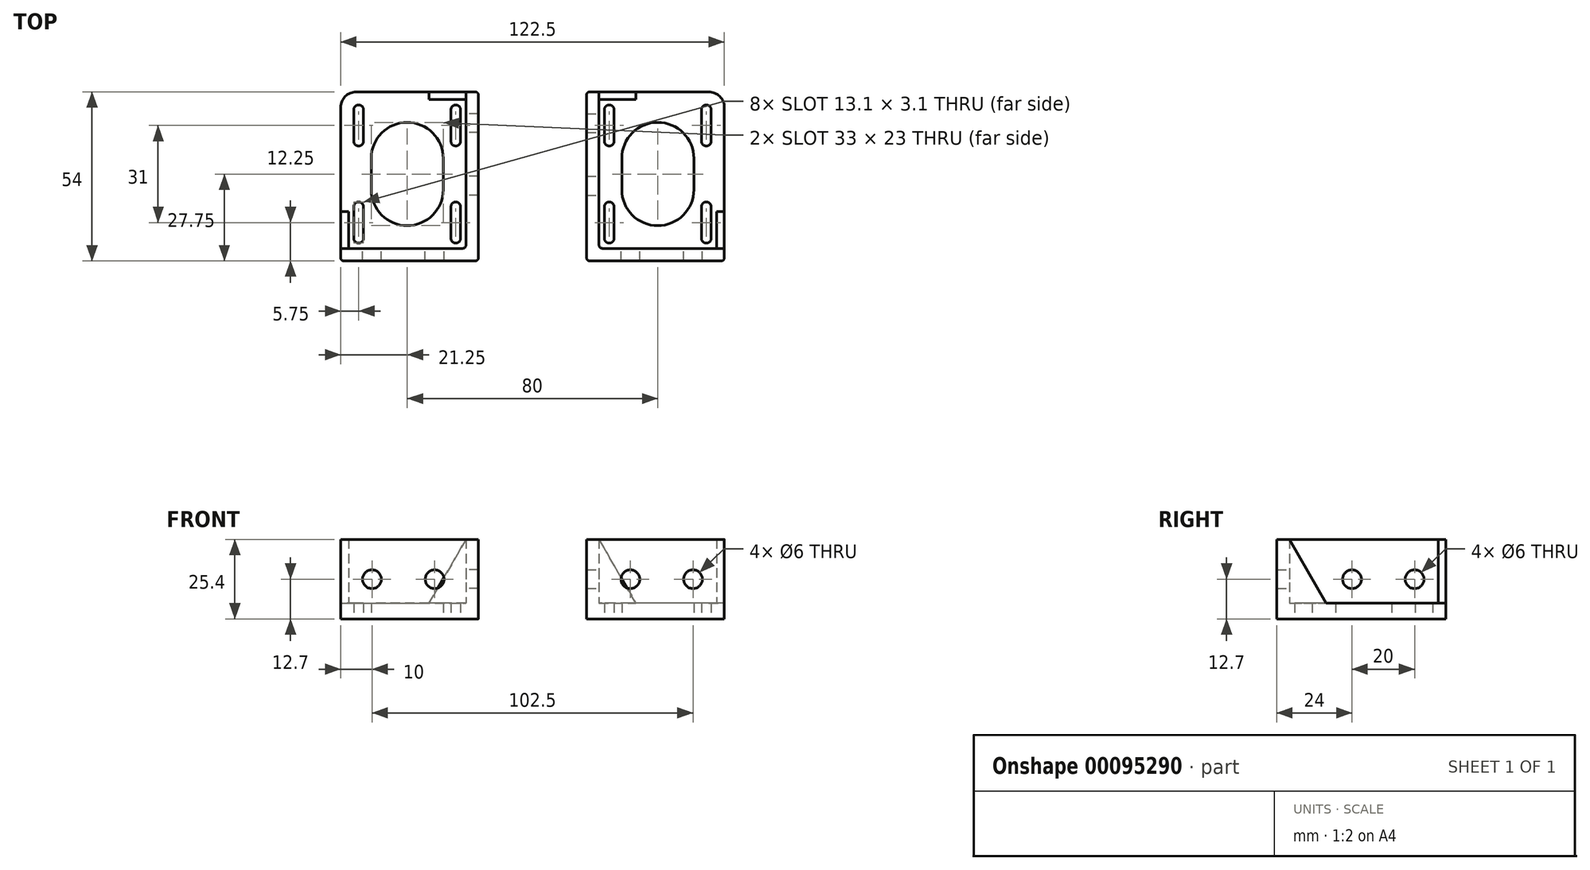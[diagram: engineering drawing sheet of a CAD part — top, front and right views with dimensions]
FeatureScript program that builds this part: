
annotation { "Feature Type Name" : "Feature", "Feature Type Description" : "" }
export const myFeature = defineFeature(function(context is Context, id is Id, definition is map)
    precondition{}
    {
        {
            var Q0;
            Q0=qCreatedBy(makeId("Top.planeOp"),FACE);
            var sketch = newSketch(context, id + "F0", { "sketchPlane" : qUnion([Q0])});
            skLineSegment(sketch, "E0.bottom", {"start": v(21.25, 31.25) * mm, "end": v(-21.25, 31.25) * mm});
            skLineSegment(sketch, "E0.top", {"start": v(21.25, -21.25) * mm, "end": v(-21.25, -21.25) * mm});
            skLineSegment(sketch, "E0.left", {"start": v(21.25, 31.25) * mm, "end": v(21.25, -21.25) * mm});
            skLineSegment(sketch, "E0.right", {"start": v(-21.25, 31.25) * mm, "end": v(-21.25, -21.25) * mm});
            skLineSegment(sketch, "E1.bottom", {"start": v(-21.25, -21.25) * mm, "end": v(21.25, -21.25) * mm});
            skLineSegment(sketch, "E1.top", {"start": v(-21.25, -22.75) * mm, "end": v(21.25, -22.75) * mm});
            skLineSegment(sketch, "E1.left", {"start": v(-21.25, -21.25) * mm, "end": v(-21.25, -22.75) * mm});
            skLineSegment(sketch, "E1.right", {"start": v(21.25, -21.25) * mm, "end": v(21.25, -22.75) * mm});
            skLineSegment(sketch, "E2.bottom", {"start": v(21.25, -22.75) * mm, "end": v(22.75, -22.75) * mm});
            skLineSegment(sketch, "E2.top", {"start": v(21.25, 31.25) * mm, "end": v(22.75, 31.25) * mm});
            skLineSegment(sketch, "E2.left", {"start": v(21.25, -22.75) * mm, "end": v(21.25, 31.25) * mm});
            skLineSegment(sketch, "E2.right", {"start": v(22.75, -22.75) * mm, "end": v(22.75, 31.25) * mm});
            skArc(sketch, "E3", {"start": v(-11.5, 0) * mm, "mid": v(0, -11.5) * mm, "end": v(11.5, 0) * mm});
            skArc(sketch, "E4", {"start": v(-17.05, -15.5) * mm, "mid": v(-15.5, -17.05) * mm, "end": v(-13.95, -15.5) * mm});
            skArc(sketch, "E5", {"start": v(-13.95, -5.5) * mm, "mid": v(-15.5, -3.95) * mm, "end": v(-17.05, -5.5) * mm});
            skLineSegment(sketch, "E6", {"start": v(-17.05, -5.5) * mm, "end": v(-17.05, -15.5) * mm});
            skLineSegment(sketch, "E7", {"start": v(-13.95, -5.5) * mm, "end": v(-13.95, -15.5) * mm});
            skLineSegment(sketch, "E8.MirrorCS", {"start": v(13.95, -5.5) * mm, "end": v(13.95, -15.5) * mm});
            skArc(sketch, "E9.MirrorCS", {"start": v(13.95, -5.5) * mm, "mid": v(15.5, -3.95) * mm, "end": v(17.05, -5.5) * mm});
            skLineSegment(sketch, "E10.MirrorCS", {"start": v(17.05, -5.5) * mm, "end": v(17.05, -15.5) * mm});
            skArc(sketch, "E11.MirrorCS", {"start": v(17.05, -15.5) * mm, "mid": v(15.5, -17.05) * mm, "end": v(13.95, -15.5) * mm});
            skArc(sketch, "E12", {"start": v(11.5, 10) * mm, "mid": v(0, 21.5) * mm, "end": v(-11.5, 10) * mm});
            skLineSegment(sketch, "E13", {"start": v(-11.5, 10) * mm, "end": v(-11.5, 0) * mm});
            skLineSegment(sketch, "E14", {"start": v(11.5, 10) * mm, "end": v(11.5, 0) * mm});
            skArc(sketch, "E15", {"start": v(-17.05, 15.5) * mm, "mid": v(-15.5, 13.95) * mm, "end": v(-13.95, 15.5) * mm});
            skArc(sketch, "E16", {"start": v(-13.95, 25.5) * mm, "mid": v(-15.5, 27.05) * mm, "end": v(-17.05, 25.5) * mm});
            skLineSegment(sketch, "E17", {"start": v(-17.05, 25.5) * mm, "end": v(-17.05, 15.5) * mm});
            skLineSegment(sketch, "E18", {"start": v(-13.95, 25.5) * mm, "end": v(-13.95, 15.5) * mm});
            skArc(sketch, "E19.MirrorCS", {"start": v(17.05, 15.5) * mm, "mid": v(15.5, 13.95) * mm, "end": v(13.95, 15.5) * mm});
            skLineSegment(sketch, "E20.MirrorCS", {"start": v(13.95, 25.5) * mm, "end": v(13.95, 15.5) * mm});
            skArc(sketch, "E21.MirrorCS", {"start": v(13.95, 25.5) * mm, "mid": v(15.5, 27.05) * mm, "end": v(17.05, 25.5) * mm});
            skLineSegment(sketch, "E22.MirrorCS", {"start": v(17.05, 25.5) * mm, "end": v(17.05, 15.5) * mm});
            skPoint(sketch, "E23", {"position": v(0, 31.25) * mm});
            skSolve(sketch);
        }
        {
            var Q0;
            Q0 = qSketchRegion(id + "F0", true);
            extrude(context, id + "F1", {"entities" : qUnion([Q0]), "depth" : 5 * mm});
        }
        {
            var Q0;
            Q0=makeQuery(id+"F1.opExtrude","CAP_FACE",FACE,{"disambiguationData":[OSD([sQuery(id+"F0.wireOp",EDGE,"E0.bottom"),sQuery(id+"F0.wireOp",EDGE,"E0.right"),sQuery(id+"F0.wireOp",EDGE,"GpWUOM2U-nNpN-jZLR-YXlT-HyPRV9s1mrvQ"),sQuery(id+"F0.wireOp",EDGE,"3giUZD7S-CY3c-reTc-bXXR-VS3OFUPkQZEU"),sQuery(id+"F0.wireOp",EDGE,"50b42f9f-af84-4361-a96d-2a7d33a850680.MirrorC"),sQuery(id+"F0.wireOp",EDGE,"375eae90-1bc9-48b0-af89-b14021c9dc740.MirrorC"),sQuery(id+"F0.wireOp",EDGE,"375eae90-1bc9-48b0-af89-b14021c9dc741.MirrorC"),sQuery(id+"F0.wireOp",EDGE,"E1.top"),sQuery(id+"F0.wireOp",EDGE,"E1.left"),sQuery(id+"F0.wireOp",EDGE,"E2.bottom"),sQuery(id+"F0.wireOp",EDGE,"E2.top"),sQuery(id+"F0.wireOp",EDGE,"E2.right")])],"isStart":false});
            var sketch = newSketch(context, id + "F2", { "sketchPlane" : qUnion([Q0])});
            skCircle(sketch, "E24", {"center": v(15.5, -15.5) * mm, "radius": 3 * mm, "construction": true});
            skLineSegment(sketch, "E25.bottom", {"start": v(-21.25, -22.75) * mm, "end": v(22.75, -22.75) * mm});
            skLineSegment(sketch, "E25.top", {"start": v(-21.25, -18.75) * mm, "end": v(22.75, -18.75) * mm});
            skLineSegment(sketch, "E25.left", {"start": v(-21.25, -22.75) * mm, "end": v(-21.25, -18.75) * mm});
            skLineSegment(sketch, "E25.right", {"start": v(22.75, -22.75) * mm, "end": v(22.75, -18.75) * mm});
            skLineSegment(sketch, "E26.bottom", {"start": v(22.75, -18.75) * mm, "end": v(18.75, -18.75) * mm});
            skLineSegment(sketch, "E26.top", {"start": v(22.75, 31.25) * mm, "end": v(18.75, 31.25) * mm});
            skLineSegment(sketch, "E26.left", {"start": v(22.75, -18.75) * mm, "end": v(22.75, 31.25) * mm});
            skLineSegment(sketch, "E26.right", {"start": v(18.75, -18.75) * mm, "end": v(18.75, 31.25) * mm});
            skLineSegment(sketch, "E27.bottom", {"start": v(-21.25, -18.75) * mm, "end": v(-18.75, -18.75) * mm});
            skLineSegment(sketch, "E27.top", {"start": v(-21.25, -7) * mm, "end": v(-18.75, -7) * mm});
            skLineSegment(sketch, "E27.left", {"start": v(-21.25, -18.75) * mm, "end": v(-21.25, -7) * mm});
            skLineSegment(sketch, "E27.right", {"start": v(-18.75, -18.75) * mm, "end": v(-18.75, -7) * mm});
            skLineSegment(sketch, "E28.bottom", {"start": v(18.75, 31.25) * mm, "end": v(7, 31.25) * mm});
            skLineSegment(sketch, "E28.top", {"start": v(18.75, 28.75) * mm, "end": v(7, 28.75) * mm});
            skLineSegment(sketch, "E28.left", {"start": v(18.75, 31.25) * mm, "end": v(18.75, 28.75) * mm});
            skLineSegment(sketch, "E28.right", {"start": v(7, 31.25) * mm, "end": v(7, 28.75) * mm});
            skSolve(sketch);
        }
        {
            var Q0;
            Q0 = qSketchRegion(id + "F2", true);
            extrude(context, id + "F3", {"entities" : qUnion([Q0]), "operationType" : NewBodyOperationType.ADD, "depth" : 20.4 * mm});
        }
        {
            var Q0;
            Q0=makeQuery(id+"F3.opExtrude","SWEPT_FACE",FACE,{"disambiguationData":[OSD([sQuery(id+"F2.wireOp",EDGE,"E25.top")])]});
            var sketch = newSketch(context, id + "F4", { "sketchPlane" : qUnion([Q0])});
            skCircle(sketch, "E29", {"center": v(11.25, 12.7) * mm, "radius": 3 * mm});
            skCircle(sketch, "E30", {"center": v(-8.75, 12.7) * mm, "radius": 3 * mm});
            skSolve(sketch);
        }
        {
            var Q0;
            Q0 = qSketchRegion(id + "F4", true);
            extrude(context, id + "F5", {"entities" : qUnion([Q0]), "operationType" : NewBodyOperationType.REMOVE, "endBound" : BoundingType.THROUGH_ALL, "oppositeDirection" : true, "depth" : 25 * mm});
        }
        {
            var Q0;
            Q0=makeQuery(id+"F3.opExtrude","SWEPT_FACE",FACE,{"disambiguationData":[OSD([sQuery(id+"F2.wireOp",EDGE,"E26.right")])]});
            var sketch = newSketch(context, id + "F6", { "sketchPlane" : qUnion([Q0])});
            skCircle(sketch, "E31", {"center": v(-1.25, 12.7) * mm, "radius": 3 * mm});
            skCircle(sketch, "E32", {"center": v(-21.25, 12.7) * mm, "radius": 3 * mm});
            skSolve(sketch);
        }
        {
            var Q0;
            Q0 = qSketchRegion(id + "F6", true);
            extrude(context, id + "F7", {"entities" : qUnion([Q0]), "operationType" : NewBodyOperationType.REMOVE, "endBound" : BoundingType.THROUGH_ALL, "oppositeDirection" : true, "depth" : 25 * mm});
        }
        {
            var Q0;
            Q0=makeQuery(id+"F3.boolean.opBoolean","MERGE",EDGE,{"derivedFrom":[makeQuery(id+"F1.opExtrude","SWEPT_EDGE",EDGE,{"disambiguationData":[OSD([sQuery(id+"F0.wireOp",EDGE,"E1.top"),sQuery(id+"F0.wireOp",EDGE,"E1.left")])]}),makeQuery(id+"F3.opExtrude","SWEPT_EDGE",EDGE,{"disambiguationData":[OSD([sQuery(id+"F2.wireOp",EDGE,"E25.bottom"),sQuery(id+"F2.wireOp",EDGE,"E25.left")])]})]});
            var Q1;
            Q1=makeQuery(id+"F3.boolean.opBoolean","MERGE",EDGE,{"derivedFrom":[makeQuery(id+"F1.opExtrude","SWEPT_EDGE",EDGE,{"disambiguationData":[OSD([sQuery(id+"F0.wireOp",EDGE,"E2.bottom"),sQuery(id+"F0.wireOp",EDGE,"E2.right")])]}),makeQuery(id+"F3.opExtrude","SWEPT_EDGE",EDGE,{"disambiguationData":[OSD([sQuery(id+"F2.wireOp",EDGE,"E25.bottom"),sQuery(id+"F2.wireOp",EDGE,"E25.right")])]})]});
            var Q2;
            Q2=makeQuery(id+"F3.boolean.opBoolean","MERGE",EDGE,{"derivedFrom":[makeQuery(id+"F1.opExtrude","SWEPT_EDGE",EDGE,{"disambiguationData":[OSD([sQuery(id+"F0.wireOp",EDGE,"E2.top"),sQuery(id+"F0.wireOp",EDGE,"E2.right")])]}),makeQuery(id+"F3.opExtrude","SWEPT_EDGE",EDGE,{"disambiguationData":[OSD([sQuery(id+"F2.wireOp",EDGE,"E26.top"),sQuery(id+"F2.wireOp",EDGE,"E26.left")])]})]});
            var Q3;
            Q3=makeQuery(id+"F3.opExtrude","SWEPT_EDGE",EDGE,{"disambiguationData":[OSD([sQuery(id+"F2.wireOp",EDGE,"E25.top"),sQuery(id+"F2.wireOp",EDGE,"E26.bottom"),sQuery(id+"F2.wireOp",EDGE,"E26.right")])]});
            fillet(context, id + "F8", {"entities" : qUnion([Q0, Q1, Q2, Q3]), "radius" : 1 * mm, "tangentPropagation" : true, "allowEdgeOverflow" : false});
        }
        {
            var Q0;
            Q0=makeQuery(id+"F1.opExtrude","SWEPT_EDGE",EDGE,{"disambiguationData":[OSD([sQuery(id+"F0.wireOp",EDGE,"E0.bottom"),sQuery(id+"F0.wireOp",EDGE,"E0.right")])]});
            fillet(context, id + "F9", {"entities" : qUnion([Q0]), "radius" : 5 * mm, "tangentPropagation" : true, "allowEdgeOverflow" : false});
        }
        {
            var Q0;
            Q0=makeQuery(id+"F3.opExtrude","CAP_EDGE",EDGE,{"disambiguationData":[OSD([sQuery(id+"F2.wireOp",EDGE,"E27.top")])],"isStart":false});
            var Q1;
            Q1=makeQuery(id+"F3.opExtrude","CAP_EDGE",EDGE,{"disambiguationData":[OSD([sQuery(id+"F2.wireOp",EDGE,"E28.right")])],"isStart":false});
            chamfer(context, id + "F10", {"entities" : qUnion([Q0, Q1]), "chamferType" : ChamferType.TWO_OFFSETS, "width1" : 20.4 * mm, "oppositeDirection" : false, "width2" : 11.75 * mm, "tangentPropagation" : true});
        }
        {
            var Q0;
            Q0=makeQuery(id+"F1.opExtrude","SWEPT_BODY",BODY,{"disambiguationData":[OSD([sQuery(id+"F0.wireOp",EDGE,"E0.bottom"),sQuery(id+"F0.wireOp",EDGE,"E0.right"),sQuery(id+"F0.wireOp",EDGE,"E1.top"),sQuery(id+"F0.wireOp",EDGE,"E1.left"),sQuery(id+"F0.wireOp",EDGE,"E2.bottom"),sQuery(id+"F0.wireOp",EDGE,"E2.top"),sQuery(id+"F0.wireOp",EDGE,"E2.right"),sQuery(id+"F0.wireOp",EDGE,"E3"),sQuery(id+"F0.wireOp",EDGE,"E4"),sQuery(id+"F0.wireOp",EDGE,"E5"),sQuery(id+"F0.wireOp",EDGE,"E6"),sQuery(id+"F0.wireOp",EDGE,"E7"),sQuery(id+"F0.wireOp",EDGE,"E8.MirrorCS"),sQuery(id+"F0.wireOp",EDGE,"E9.MirrorCS"),sQuery(id+"F0.wireOp",EDGE,"E10.MirrorCS"),sQuery(id+"F0.wireOp",EDGE,"E11.MirrorCS"),sQuery(id+"F0.wireOp",EDGE,"E12"),sQuery(id+"F0.wireOp",EDGE,"E13"),sQuery(id+"F0.wireOp",EDGE,"E14"),sQuery(id+"F0.wireOp",EDGE,"E15"),sQuery(id+"F0.wireOp",EDGE,"E16"),sQuery(id+"F0.wireOp",EDGE,"E17"),sQuery(id+"F0.wireOp",EDGE,"E18"),sQuery(id+"F0.wireOp",EDGE,"E19.MirrorCS"),sQuery(id+"F0.wireOp",EDGE,"E20.MirrorCS"),sQuery(id+"F0.wireOp",EDGE,"E21.MirrorCS"),sQuery(id+"F0.wireOp",EDGE,"E22.MirrorCS")])]});
            var Q1;
            Q1=qCreatedBy(makeId("Right.planeOp"),FACE);
            mirror(context, id + "F11", {"entities" : qUnion([Q0]), "mirrorPlane" : qUnion([Q1])});
        }
        {
            var Q0;
            Q0=makeQuery(id+"F11.opPattern","COPY",BODY,{"derivedFrom":makeQuery(id+"F1.opExtrude","SWEPT_BODY",BODY,{"disambiguationData":[OSD([sQuery(id+"F0.wireOp",EDGE,"E0.bottom"),sQuery(id+"F0.wireOp",EDGE,"E0.right"),sQuery(id+"F0.wireOp",EDGE,"E1.top"),sQuery(id+"F0.wireOp",EDGE,"E1.left"),sQuery(id+"F0.wireOp",EDGE,"E2.bottom"),sQuery(id+"F0.wireOp",EDGE,"E2.top"),sQuery(id+"F0.wireOp",EDGE,"E2.right"),sQuery(id+"F0.wireOp",EDGE,"E3"),sQuery(id+"F0.wireOp",EDGE,"E4"),sQuery(id+"F0.wireOp",EDGE,"E5"),sQuery(id+"F0.wireOp",EDGE,"E6"),sQuery(id+"F0.wireOp",EDGE,"E7"),sQuery(id+"F0.wireOp",EDGE,"E8.MirrorCS"),sQuery(id+"F0.wireOp",EDGE,"E9.MirrorCS"),sQuery(id+"F0.wireOp",EDGE,"E10.MirrorCS"),sQuery(id+"F0.wireOp",EDGE,"E11.MirrorCS"),sQuery(id+"F0.wireOp",EDGE,"E12"),sQuery(id+"F0.wireOp",EDGE,"E13"),sQuery(id+"F0.wireOp",EDGE,"E14"),sQuery(id+"F0.wireOp",EDGE,"E15"),sQuery(id+"F0.wireOp",EDGE,"E16"),sQuery(id+"F0.wireOp",EDGE,"E17"),sQuery(id+"F0.wireOp",EDGE,"E18"),sQuery(id+"F0.wireOp",EDGE,"E19.MirrorCS"),sQuery(id+"F0.wireOp",EDGE,"E20.MirrorCS"),sQuery(id+"F0.wireOp",EDGE,"E21.MirrorCS"),sQuery(id+"F0.wireOp",EDGE,"E22.MirrorCS")])]}),"instanceName":"1"});
            var Q1;
            Q1=qCreatedBy(makeId("Right.planeOp"),FACE);
            transform(context, id + "F12", {"entities" : qUnion([Q0]), "transformType" : TransformType.TRANSLATION_DISTANCE, "transformDirection" : qUnion([Q1]), "distance" : 80 * mm, "makeCopy" : false});
        }
    });
